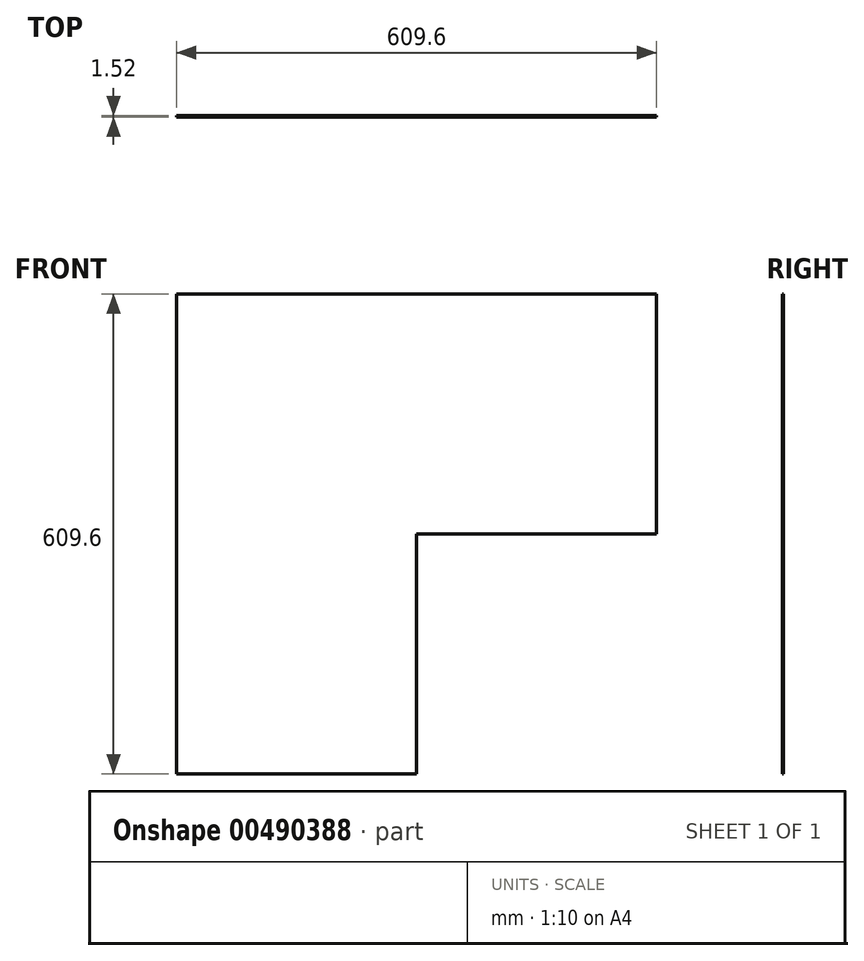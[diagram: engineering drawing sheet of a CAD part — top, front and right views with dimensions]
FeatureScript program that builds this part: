
annotation { "Feature Type Name" : "Feature", "Feature Type Description" : "" }
export const myFeature = defineFeature(function(context is Context, id is Id, definition is map)
    precondition{}
    {
        {
            var Q0;
            Q0=qCreatedBy(makeId("Front.planeOp"),FACE);
            var sketch = newSketch(context, id + "F0", { "sketchPlane" : qUnion([Q0])});
            skLineSegment(sketch, "E0.bottom", {"start": v(-304.8, 0) * mm, "end": v(-609.6, 0) * mm});
            skLineSegment(sketch, "E0.top", {"start": v(0, 609.6) * mm, "end": v(-609.6, 609.6) * mm});
            skLineSegment(sketch, "E0.left", {"start": v(0, 304.8) * mm, "end": v(0, 609.6) * mm});
            skLineSegment(sketch, "E0.right", {"start": v(-609.6, 0) * mm, "end": v(-609.6, 609.6) * mm});
            skLineSegment(sketch, "E1.top", {"start": v(0, 304.8) * mm, "end": v(-304.8, 304.8) * mm});
            skLineSegment(sketch, "E1.right", {"start": v(-304.8, 0) * mm, "end": v(-304.8, 304.8) * mm});
            skSolve(sketch);
        }
        {
            var Q0;
            Q0 = qSketchRegion(id + "F0", true);
            extrude(context, id + "F1", {"entities" : qUnion([Q0]), "depth" : 1.52 * mm});
        }
    });
